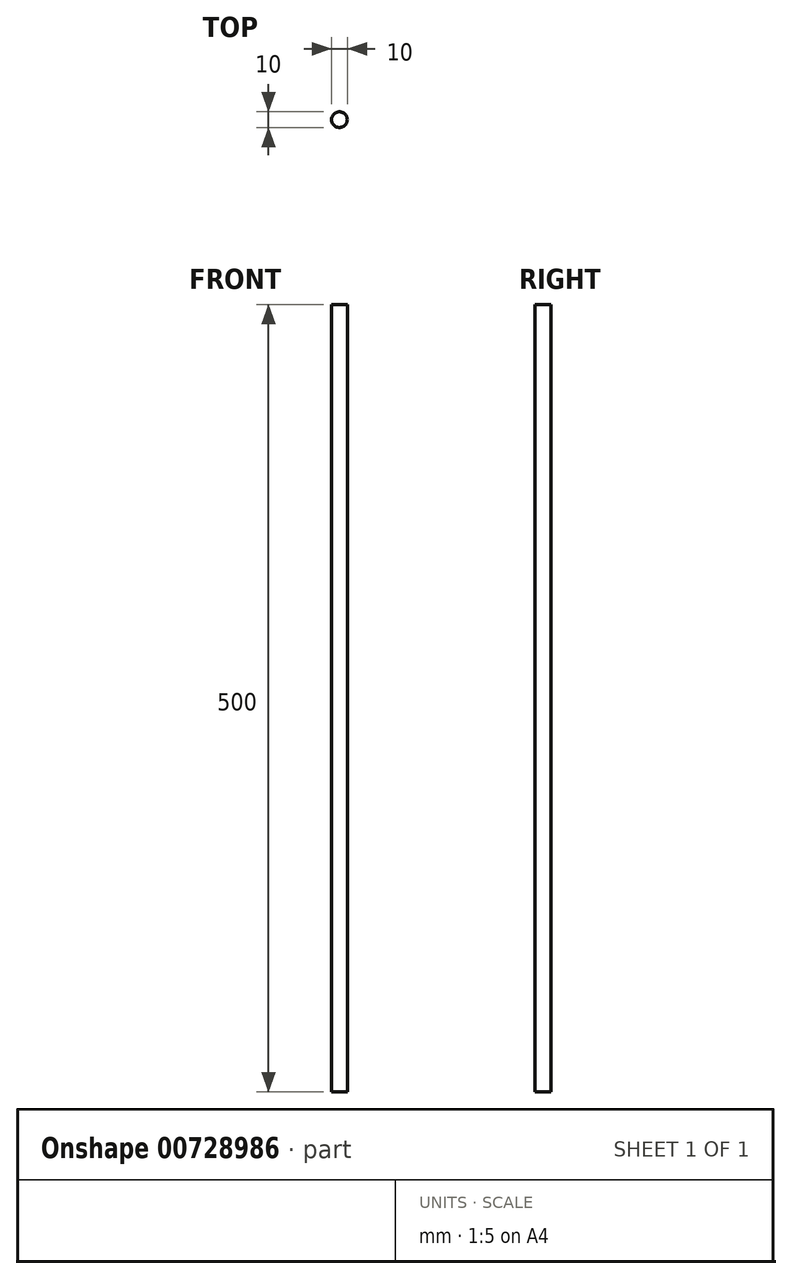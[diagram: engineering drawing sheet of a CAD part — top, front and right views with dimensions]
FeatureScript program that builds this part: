
annotation { "Feature Type Name" : "Feature", "Feature Type Description" : "" }
export const myFeature = defineFeature(function(context is Context, id is Id, definition is map)
    precondition{}
    {
        {
            var Q0;
            Q0=qCreatedBy(makeId("Top.planeOp"),FACE);
            var sketch = newSketch(context, id + "F0", { "sketchPlane" : qUnion([Q0])});
            skCircle(sketch, "E0", {"center": v(1.57, 0) * mm, "radius": 5 * mm});
            skSolve(sketch);
        }
        {
            var Q0;
            Q0=makeQuery(id+"F0.imprint","IMPRINT",FACE,{"disambiguationData":[TD([[makeQuery(id+"F0.imprint","IMPRINT",EDGE,{"derivedFrom":sQuery(id+"F0.wireOp",EDGE,"E0")}),1.0]])]});
            extrude(context, id + "F1", {"entities" : qUnion([Q0]), "depth" : 500 * mm, "offsetDistance" : 25 * mm});
        }
    });
